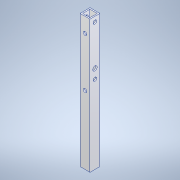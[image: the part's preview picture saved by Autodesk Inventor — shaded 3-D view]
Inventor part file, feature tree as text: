
AUTODESK INVENTOR PART (.ipt)
format: ipt  version: 2020.3 (Build 243373000, 373)  size: 151,552 bytes
history: native  units: mm
features: sketch x5, hole x3, extrude x2, other x1
ambient origin geometry x8: Origin, YZ Plane, XZ Plane, XY Plane, X Axis, Y Axis, Z Axis, Center Point
bodies: Body1 (feature_tree)
feature tree (11):
  other  "ソリッド1"
  extrude  "押し出し1"  Depth=9.0mm
  hole  "穴2"  [1 undecoded]
  hole  "穴3"  [1 undecoded]
  hole  "穴4"  [1 undecoded]
  extrude  "押し出し2"  Depth=1.2mm
  sketch  "スケッチ1"
  sketch  "スケッチ3"
  sketch  "スケッチ4"
  sketch  "スケッチ5"
  sketch  "スケッチ6"
note: 3 required parameter values undecoded (feature->parameter linkage not recoverable at this tier; creation-order binding heuristic only, values carry confidence <= 0.55)
